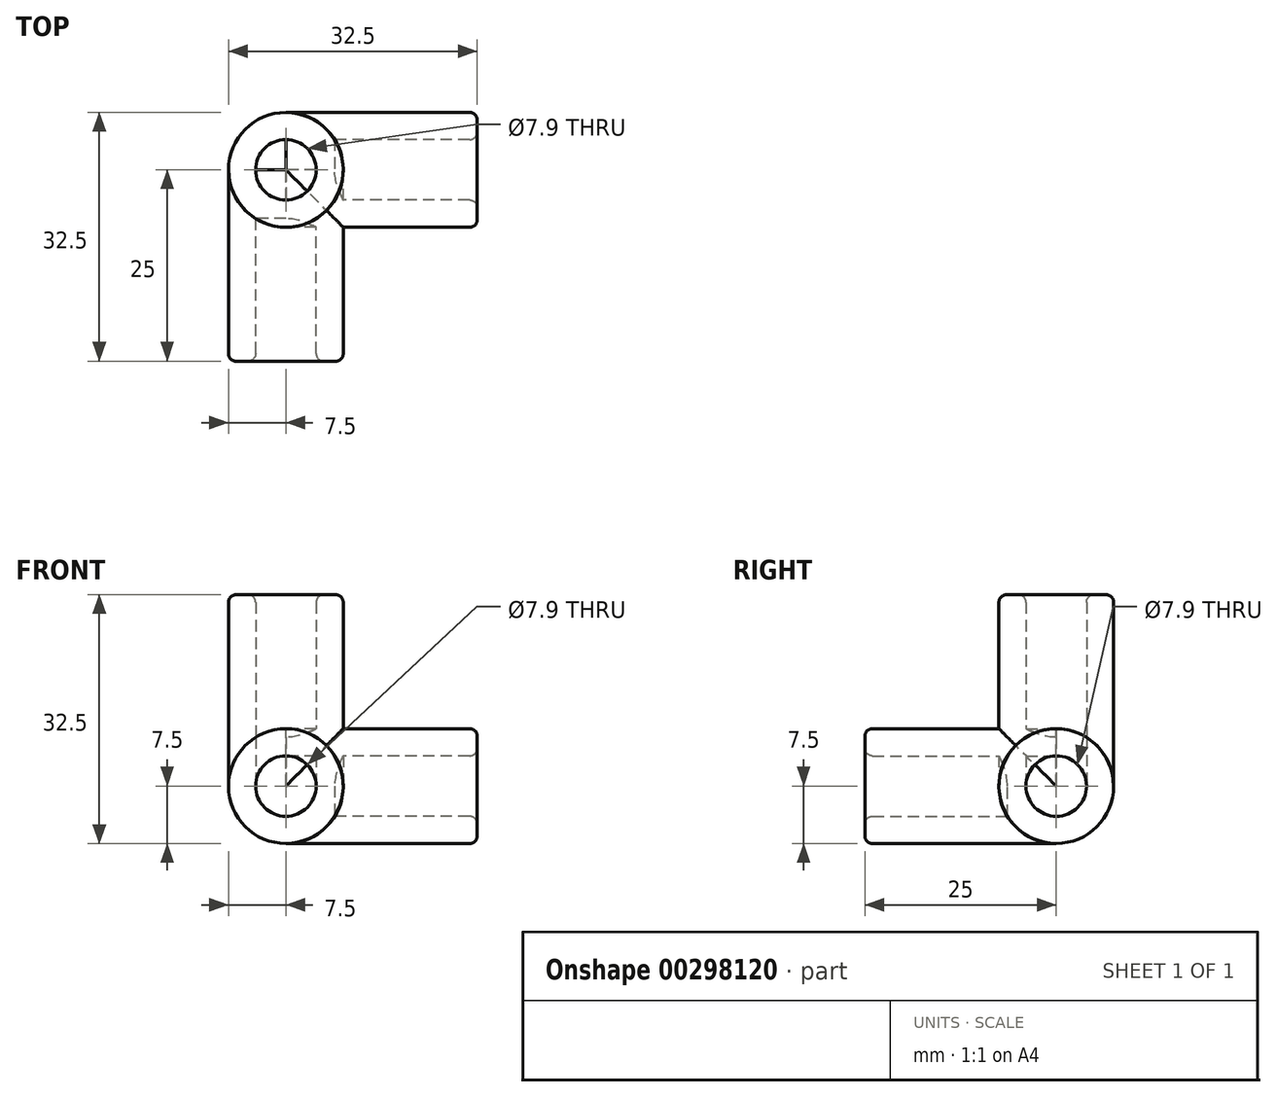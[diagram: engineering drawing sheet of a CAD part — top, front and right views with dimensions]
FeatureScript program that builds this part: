
annotation { "Feature Type Name" : "Feature", "Feature Type Description" : "" }
export const myFeature = defineFeature(function(context is Context, id is Id, definition is map)
    precondition{}
    {
        {
            var Q0;
            Q0=qCreatedBy(makeId("Top.planeOp"),FACE);
            var sketch = newSketch(context, id + "F0", { "sketchPlane" : qUnion([Q0])});
            skCircle(sketch, "E0", {"center": v(0, 0) * mm, "radius": 3.95 * mm});
            skCircle(sketch, "E1", {"center": v(0, 0) * mm, "radius": 7.5 * mm});
            skSolve(sketch);
        }
        {
            var Q0;
            Q0=qCreatedBy(makeId("Right.planeOp"),FACE);
            var sketch = newSketch(context, id + "F1", { "sketchPlane" : qUnion([Q0])});
            skCircle(sketch, "E2", {"center": v(0, 0) * mm, "radius": 3.95 * mm});
            skCircle(sketch, "E3", {"center": v(0, 0) * mm, "radius": 7.5 * mm});
            skSolve(sketch);
        }
        {
            var Q0;
            Q0=qCreatedBy(makeId("Front.planeOp"),FACE);
            var sketch = newSketch(context, id + "F2", { "sketchPlane" : qUnion([Q0])});
            skCircle(sketch, "E4", {"center": v(0, 0) * mm, "radius": 3.95 * mm});
            skCircle(sketch, "E5", {"center": v(0, 0) * mm, "radius": 7.5 * mm});
            skSolve(sketch);
        }
        {
            var Q0;
            Q0=makeQuery(id+"F2.imprint","IMPRINT",FACE,{"disambiguationData":[TD([[makeQuery(id+"F2.imprint","IMPRINT",EDGE,{"derivedFrom":sQuery(id+"F2.wireOp",EDGE,"E4")}),-1.0]])]});
            extrude(context, id + "F3", {"entities" : qUnion([Q0]), "depth" : 25 * mm});
        }
        {
            var Q0;
            Q0=makeQuery(id+"F1.imprint","IMPRINT",FACE,{"disambiguationData":[TD([[makeQuery(id+"F1.imprint","IMPRINT",EDGE,{"derivedFrom":sQuery(id+"F1.wireOp",EDGE,"E2")}),-1.0]])]});
            extrude(context, id + "F4", {"entities" : qUnion([Q0]), "operationType" : NewBodyOperationType.ADD, "depth" : 25 * mm});
        }
        {
            var Q0;
            Q0=makeQuery(id+"F0.imprint","IMPRINT",FACE,{"disambiguationData":[TD([[makeQuery(id+"F0.imprint","IMPRINT",EDGE,{"derivedFrom":sQuery(id+"F0.wireOp",EDGE,"E0")}),-1.0]])]});
            extrude(context, id + "F5", {"entities" : qUnion([Q0]), "operationType" : NewBodyOperationType.ADD, "depth" : 25 * mm});
        }
        {
            var Q0;
            {var subQ0=sQuery(id+"F2.wireOp",EDGE,"E5");var subQ1=makeQuery(id+"F3.opExtrude","SWEPT_FACE",FACE,{"disambiguationData":[OSD([subQ0])]});var subQ2=sQuery(id+"F1.wireOp",EDGE,"E2");var subQ3=makeQuery(id+"F4.opExtrude","SWEPT_FACE",FACE,{"disambiguationData":[OSD([subQ2])]});var subQ4=sQuery(id+"F0.wireOp",EDGE,"E1");var subQ5=sQuery(id+"F2.wireOp",EDGE,"E4");var subQ6=makeQuery(id+"F3.opExtrude","CAP_FACE",FACE,{"disambiguationData":[OSD([subQ5,subQ0])],"isStart":true});var subQ7=sQuery(id+"F0.wireOp",EDGE,"E0");var subQ8=makeQuery(id+"F3.opExtrude","SWEPT_FACE",FACE,{"disambiguationData":[OSD([subQ5])]});var subQ9=sQuery(id+"F1.wireOp",EDGE,"E3");var subQ10=makeQuery(id+"F4.opExtrude","CAP_FACE",FACE,{"disambiguationData":[OSD([subQ2,subQ9])],"isStart":true});var subQ11=makeQuery(id+"F4.opExtrude","SWEPT_FACE",FACE,{"disambiguationData":[OSD([subQ9])]});Q0=makeQuery(id+"F5.boolean.opBoolean","SPLIT",FACE,{"disambiguationData":[TD([subQ8,subQ6,subQ1,subQ3,subQ10,subQ11,makeQuery(id+"F5.opExtrude","SWEPT_FACE",FACE,{"disambiguationData":[OSD([subQ7])]}),makeQuery(id+"F5.opExtrude","CAP_FACE",FACE,{"disambiguationData":[OSD([subQ7,subQ4])],"isStart":true}),makeQuery(id+"F5.opExtrude","SWEPT_FACE",FACE,{"disambiguationData":[OSD([subQ4])]})])],"derivedFrom":makeQuery(id+"F4.boolean.opBoolean","SPLIT",FACE,{"disambiguationData":[TD([subQ8,subQ6,subQ1,subQ3,subQ10,subQ11])],"derivedFrom":subQ6})});}
            var Q1;
            Q1=makeQuery(id+"F4.boolean.opBoolean","INTERSECT",EDGE,{"disambiguationData":[OD(0.0)],"derivedFrom":[makeQuery(id+"F3.opExtrude","CAP_FACE",FACE,{"disambiguationData":[OSD([sQuery(id+"F2.wireOp",EDGE,"E4"),sQuery(id+"F2.wireOp",EDGE,"E5")])],"isStart":true}),makeQuery(id+"F4.opExtrude","CAP_FACE",FACE,{"disambiguationData":[OSD([sQuery(id+"F1.wireOp",EDGE,"E2"),sQuery(id+"F1.wireOp",EDGE,"E3")])],"isStart":true})]});
            revolve(context, id + "F6", {"operationType" : NewBodyOperationType.ADD, "entities" : qUnion([Q0]), "axis" : qUnion([Q1]), "revolveType" : RevolveType.FULL});
        }
        {
            var Q0;
            Q0=makeQuery(id+"F4.opExtrude","CAP_EDGE",EDGE,{"disambiguationData":[OSD([sQuery(id+"F1.wireOp",EDGE,"E2")])],"isStart":false});
            var Q1;
            Q1=makeQuery(id+"F4.opExtrude","CAP_EDGE",EDGE,{"disambiguationData":[OSD([sQuery(id+"F1.wireOp",EDGE,"E3")])],"isStart":false});
            var Q2;
            Q2=makeQuery(id+"F3.opExtrude","CAP_EDGE",EDGE,{"disambiguationData":[OSD([sQuery(id+"F2.wireOp",EDGE,"E4")])],"isStart":false});
            var Q3;
            Q3=makeQuery(id+"F3.opExtrude","CAP_EDGE",EDGE,{"disambiguationData":[OSD([sQuery(id+"F2.wireOp",EDGE,"E5")])],"isStart":false});
            var Q4;
            Q4=makeQuery(id+"F5.opExtrude","CAP_EDGE",EDGE,{"disambiguationData":[OSD([sQuery(id+"F0.wireOp",EDGE,"E0")])],"isStart":false});
            var Q5;
            Q5=makeQuery(id+"F5.opExtrude","CAP_EDGE",EDGE,{"disambiguationData":[OSD([sQuery(id+"F0.wireOp",EDGE,"E1")])],"isStart":false});
            fillet(context, id + "F7", {"entities" : qUnion([Q0, Q1, Q2, Q3, Q4, Q5]), "radius" : 1 * mm, "tangentPropagation" : true, "allowEdgeOverflow" : false});
        }
    });
